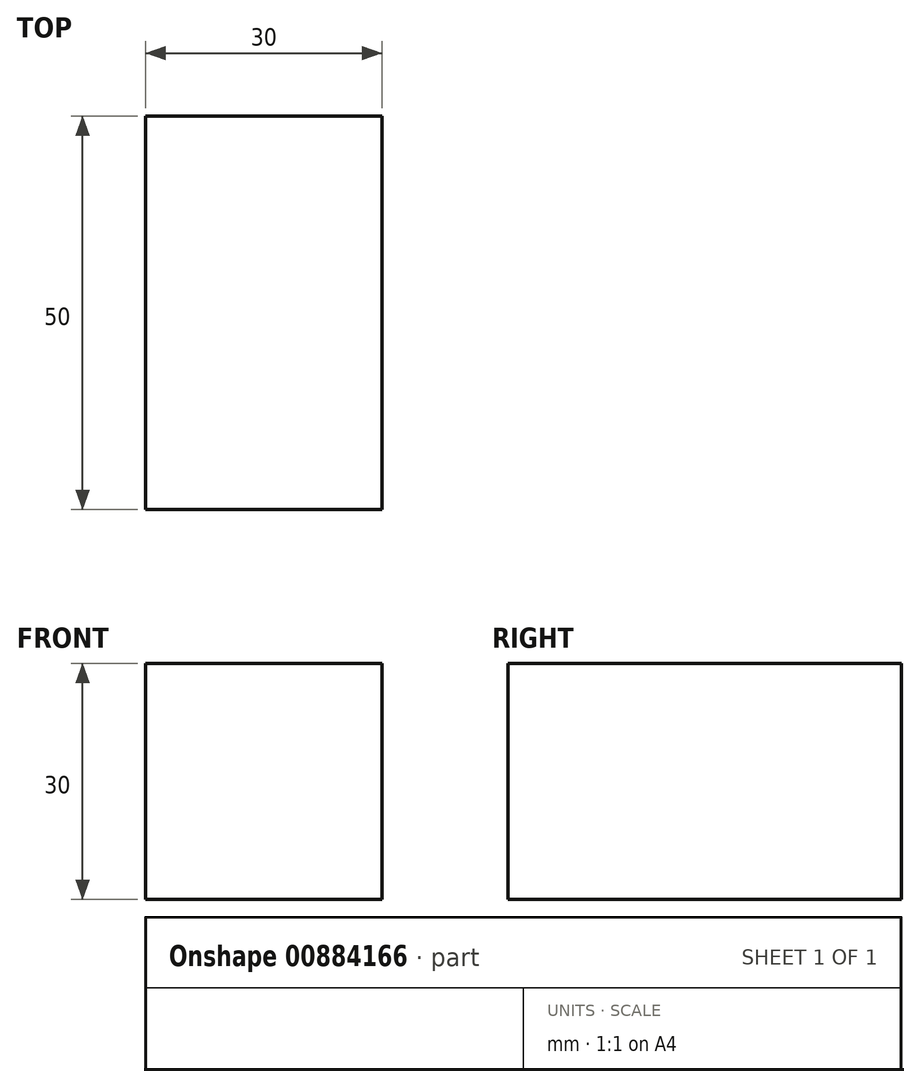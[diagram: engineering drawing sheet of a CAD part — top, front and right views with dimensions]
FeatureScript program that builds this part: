
annotation { "Feature Type Name" : "Feature", "Feature Type Description" : "" }
export const myFeature = defineFeature(function(context is Context, id is Id, definition is map)
    precondition{}
    {
        {
            var Q0;
            Q0=qCreatedBy(makeId("Front.planeOp"),FACE);
            var sketch = newSketch(context, id + "F0", { "sketchPlane" : qUnion([Q0])});
            skLineSegment(sketch, "E0.bottom", {"start": v(0, 0) * mm, "end": v(30, 0) * mm});
            skLineSegment(sketch, "E0.top", {"start": v(0, 30) * mm, "end": v(30, 30) * mm});
            skLineSegment(sketch, "E0.left", {"start": v(0, 0) * mm, "end": v(0, 30) * mm});
            skLineSegment(sketch, "E0.right", {"start": v(30, 0) * mm, "end": v(30, 30) * mm});
            skSolve(sketch);
        }
        {
            var Q0;
            Q0 = qSketchRegion(id + "F0", true);
            extrude(context, id + "F1", {"entities" : qUnion([Q0]), "depth" : 50 * mm, "offsetDistance" : 25 * mm});
        }
    });
